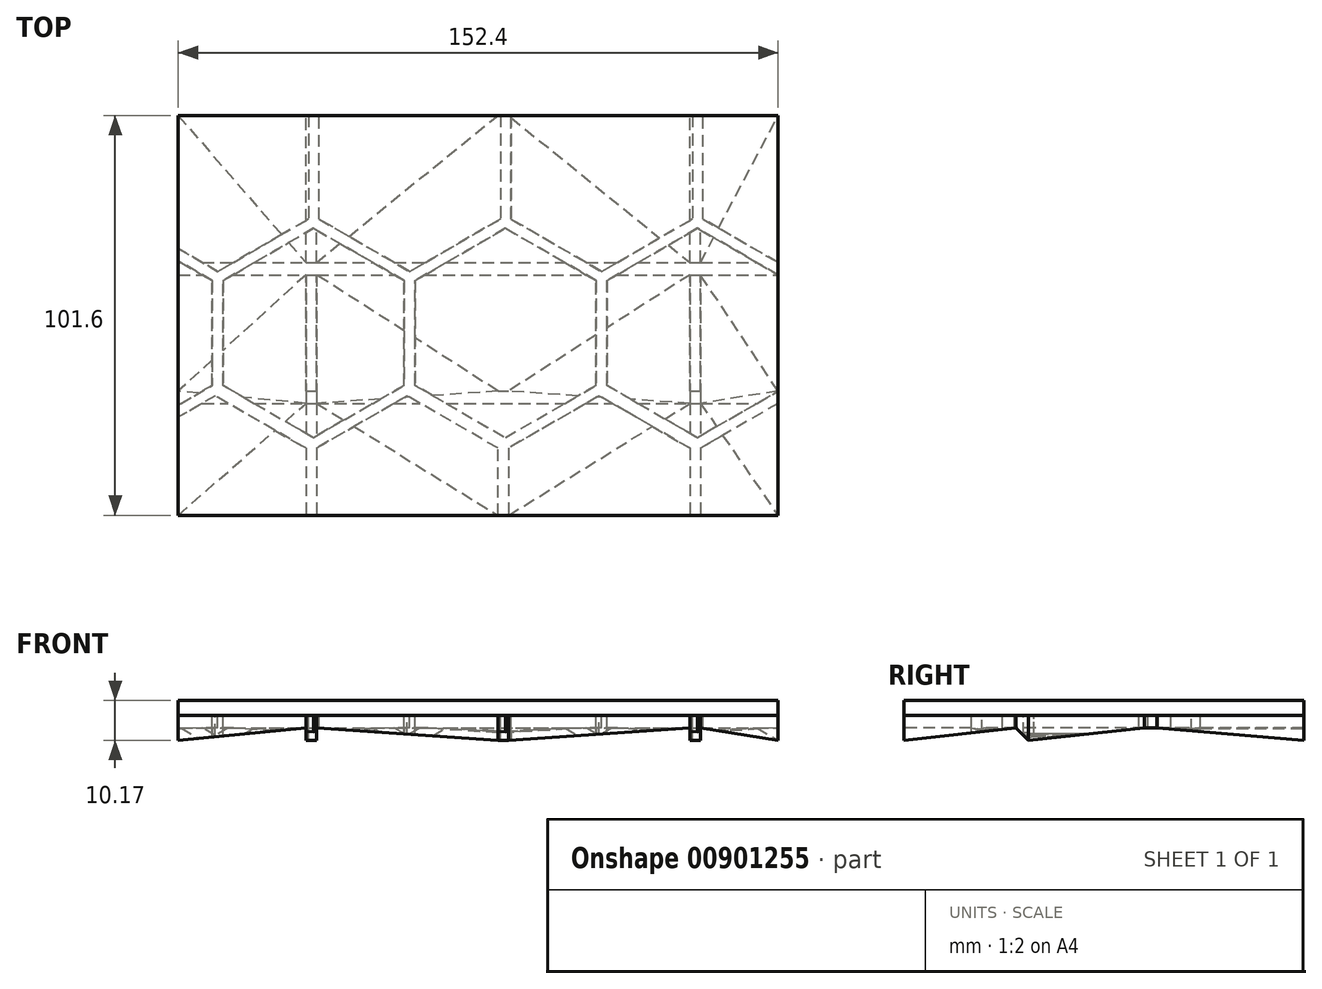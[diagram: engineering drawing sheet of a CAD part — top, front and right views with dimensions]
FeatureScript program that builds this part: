
annotation { "Feature Type Name" : "Feature", "Feature Type Description" : "" }
export const myFeature = defineFeature(function(context is Context, id is Id, definition is map)
    precondition{}
    {
        {
            var Q0;
            Q0=qCreatedBy(makeId("Top.planeOp"),FACE);
            var sketch = newSketch(context, id + "F0", { "sketchPlane" : qUnion([Q0])});
            skLineSegment(sketch, "E0.bottom", {"start": v(-65.42, 49.7) * mm, "end": v(86.98, 49.7) * mm});
            skLineSegment(sketch, "E0.top", {"start": v(-65.42, -51.9) * mm, "end": v(86.98, -51.9) * mm});
            skLineSegment(sketch, "E0.left", {"start": v(-65.42, 49.7) * mm, "end": v(-65.42, -51.9) * mm});
            skLineSegment(sketch, "E0.right", {"start": v(86.98, 49.7) * mm, "end": v(86.98, -51.9) * mm});
            skCircle(sketch, "E1", {"center": v(-62.35, 45.98) * mm, "radius": 11.46 * mm});
            skSolve(sketch);
        }
        {
            var Q0;
            {var subQ2=sQuery(id+"F0.wireOp",EDGE,"E0.top");Q0=makeQuery(id+"F0.imprint","IMPRINT",FACE,{"disambiguationData":[TD([[makeQuery(id+"F0.imprint","IMPRINT",EDGE,{"derivedFrom":subQ2}),1.0]])]});}
            var Q1;
            {var subQ0=sQuery(id+"F0.wireOp",EDGE,"E0.left");var subQ1=sQuery(id+"F0.wireOp",EDGE,"E0.bottom");var subQ2=makeQuery(id+"F0.imprint","INTERSECT",VERTEX,{"derivedFrom":[subQ1,subQ0]});Q1=makeQuery(id+"F0.imprint","IMPRINT",FACE,{"disambiguationData":[TD([[makeQuery(id+"F0.imprint","IMPRINT",EDGE,{"disambiguationData":[TD([[subQ2,-1.0]])],"derivedFrom":subQ1}),-1.0]])]});}
            extrude(context, id + "F1", {"entities" : qUnion([Q0, Q1]), "endBound" : BoundingType.SYMMETRIC, "oppositeDirection" : true, "depth" : 3.8 * mm, "offsetDistance" : 25.4 * mm});
        }
        {
            var Q0;
            Q0=makeQuery(id+"F1.opExtrude","CAP_FACE",FACE,{"disambiguationData":[OSD([sQuery(id+"F0.wireOp",EDGE,"E0.bottom"),sQuery(id+"F0.wireOp",EDGE,"E0.top"),sQuery(id+"F0.wireOp",EDGE,"E0.left"),sQuery(id+"F0.wireOp",EDGE,"E0.right")])],"isStart":false});
            var sketch = newSketch(context, id + "F2", { "sketchPlane" : qUnion([Q0])});
            skCircle(sketch, "E2.cCircle", {"center": v(-56.01, 48.13) * mm, "radius": 23.03 * mm, "construction": true});
            skLineSegment(sketch, "E2.0", {"start": v(-32.98, 34.83) * mm, "end": v(-56.01, 21.53) * mm});
            skLineSegment(sketch, "E2.1", {"start": v(-56.01, 21.53) * mm, "end": v(-79.04, 34.83) * mm});
            skLineSegment(sketch, "E2.2", {"start": v(-79.04, 34.83) * mm, "end": v(-79.04, 61.43) * mm});
            skLineSegment(sketch, "E2.3", {"start": v(-79.04, 61.43) * mm, "end": v(-56.01, 74.72) * mm});
            skLineSegment(sketch, "E2.4", {"start": v(-56.01, 74.72) * mm, "end": v(-32.98, 61.43) * mm});
            skLineSegment(sketch, "E2.5", {"start": v(-32.98, 61.43) * mm, "end": v(-32.98, 34.83) * mm});
            skPoint(sketch, "E2.0.midPoint", {"position": v(-44.5, 28.18) * mm});
            skLineSegment(sketch, "E3", {"start": v(-56.01, 48.13) * mm, "end": v(-56.01, 21.53) * mm});
            skLineSegment(sketch, "E4.0.1.0", {"start": v(-32.34, -49.95) * mm, "end": v(-55.37, -63.25) * mm});
            skLineSegment(sketch, "E4.0.1.1", {"start": v(-55.37, -63.25) * mm, "end": v(-78.4, -49.95) * mm});
            skLineSegment(sketch, "E4.0.1.2", {"start": v(-78.4, -49.95) * mm, "end": v(-78.4, -23.35) * mm});
            skLineSegment(sketch, "E4.0.1.3", {"start": v(-78.4, -23.35) * mm, "end": v(-55.37, -10.05) * mm});
            skLineSegment(sketch, "E4.0.1.4", {"start": v(-55.37, -10.05) * mm, "end": v(-32.34, -23.35) * mm});
            skLineSegment(sketch, "E4.0.1.5", {"start": v(-32.34, -23.35) * mm, "end": v(-32.34, -49.95) * mm});
            skLineSegment(sketch, "E4.1.0.0", {"start": v(15.79, 34.83) * mm, "end": v(-7.24, 21.53) * mm});
            skLineSegment(sketch, "E4.1.0.1", {"start": v(-7.24, 21.53) * mm, "end": v(-30.28, 34.83) * mm});
            skLineSegment(sketch, "E4.1.0.2", {"start": v(-30.28, 34.83) * mm, "end": v(-30.28, 61.43) * mm});
            skLineSegment(sketch, "E4.1.0.3", {"start": v(-30.28, 61.43) * mm, "end": v(-7.24, 74.72) * mm});
            skLineSegment(sketch, "E4.1.0.4", {"start": v(-7.24, 74.72) * mm, "end": v(15.79, 61.43) * mm});
            skLineSegment(sketch, "E4.1.0.5", {"start": v(15.79, 61.43) * mm, "end": v(15.79, 34.83) * mm});
            skLineSegment(sketch, "E4.1.1.0", {"start": v(16.43, -49.95) * mm, "end": v(-6.6, -63.25) * mm});
            skLineSegment(sketch, "E4.1.1.1", {"start": v(-6.6, -63.25) * mm, "end": v(-29.64, -49.95) * mm});
            skLineSegment(sketch, "E4.1.1.2", {"start": v(-29.64, -49.95) * mm, "end": v(-29.64, -23.35) * mm});
            skLineSegment(sketch, "E4.1.1.3", {"start": v(-29.64, -23.35) * mm, "end": v(-6.6, -10.05) * mm});
            skLineSegment(sketch, "E4.1.1.4", {"start": v(-6.6, -10.05) * mm, "end": v(16.43, -23.35) * mm});
            skLineSegment(sketch, "E4.1.1.5", {"start": v(16.43, -23.35) * mm, "end": v(16.43, -49.95) * mm});
            skLineSegment(sketch, "E4.2.0.0", {"start": v(64.56, 34.83) * mm, "end": v(41.52, 21.53) * mm});
            skLineSegment(sketch, "E4.2.0.1", {"start": v(41.52, 21.53) * mm, "end": v(18.5, 34.83) * mm});
            skLineSegment(sketch, "E4.2.0.2", {"start": v(18.5, 34.83) * mm, "end": v(18.5, 61.43) * mm});
            skLineSegment(sketch, "E4.2.0.3", {"start": v(18.5, 61.43) * mm, "end": v(41.52, 74.72) * mm});
            skLineSegment(sketch, "E4.2.0.4", {"start": v(41.52, 74.72) * mm, "end": v(64.56, 61.43) * mm});
            skLineSegment(sketch, "E4.2.0.5", {"start": v(64.56, 61.43) * mm, "end": v(64.56, 34.83) * mm});
            skLineSegment(sketch, "E4.2.1.0", {"start": v(65.2, -49.95) * mm, "end": v(42.16, -63.25) * mm});
            skLineSegment(sketch, "E4.2.1.1", {"start": v(42.16, -63.25) * mm, "end": v(19.13, -49.95) * mm});
            skLineSegment(sketch, "E4.2.1.2", {"start": v(19.13, -49.95) * mm, "end": v(19.13, -23.35) * mm});
            skLineSegment(sketch, "E4.2.1.3", {"start": v(19.13, -23.35) * mm, "end": v(42.16, -10.05) * mm});
            skLineSegment(sketch, "E4.2.1.4", {"start": v(42.16, -10.05) * mm, "end": v(65.2, -23.35) * mm});
            skLineSegment(sketch, "E4.2.1.5", {"start": v(65.2, -23.35) * mm, "end": v(65.2, -49.95) * mm});
            skLineSegment(sketch, "E4.3.0.0", {"start": v(113.33, 34.83) * mm, "end": v(90.3, 21.53) * mm});
            skLineSegment(sketch, "E4.3.0.1", {"start": v(90.3, 21.53) * mm, "end": v(67.26, 34.83) * mm});
            skLineSegment(sketch, "E4.3.0.2", {"start": v(67.26, 34.83) * mm, "end": v(67.26, 61.43) * mm});
            skLineSegment(sketch, "E4.3.0.3", {"start": v(67.26, 61.43) * mm, "end": v(90.3, 74.72) * mm});
            skLineSegment(sketch, "E4.3.0.4", {"start": v(90.3, 74.72) * mm, "end": v(113.33, 61.43) * mm});
            skLineSegment(sketch, "E4.3.0.5", {"start": v(113.33, 61.43) * mm, "end": v(113.33, 34.83) * mm});
            skLineSegment(sketch, "E4.3.1.0", {"start": v(113.97, -49.95) * mm, "end": v(90.93, -63.25) * mm});
            skLineSegment(sketch, "E4.3.1.1", {"start": v(90.93, -63.25) * mm, "end": v(67.9, -49.95) * mm});
            skLineSegment(sketch, "E4.3.1.2", {"start": v(67.9, -49.95) * mm, "end": v(67.9, -23.35) * mm});
            skLineSegment(sketch, "E4.3.1.3", {"start": v(67.9, -23.35) * mm, "end": v(90.93, -10.05) * mm});
            skLineSegment(sketch, "E4.3.1.4", {"start": v(90.93, -10.05) * mm, "end": v(113.97, -23.35) * mm});
            skLineSegment(sketch, "E4.3.1.5", {"start": v(113.97, -23.35) * mm, "end": v(113.97, -49.95) * mm});
            skLineSegment(sketch, "E4.direction1", {"start": v(-56.01, 21.53) * mm, "end": v(-7.24, 21.53) * mm, "construction": true});
            skLineSegment(sketch, "E4.direction2", {"start": v(-56.01, 21.53) * mm, "end": v(-55.37, -63.25) * mm, "construction": true});
            skCircle(sketch, "E5.cCircle", {"center": v(-79.8, 5.56) * mm, "radius": 23.03 * mm, "construction": true});
            skLineSegment(sketch, "E5.0", {"start": v(-56.77, -7.74) * mm, "end": v(-79.8, -21.04) * mm});
            skLineSegment(sketch, "E5.1", {"start": v(-79.8, -21.04) * mm, "end": v(-102.83, -7.74) * mm});
            skLineSegment(sketch, "E5.2", {"start": v(-102.83, -7.74) * mm, "end": v(-102.83, 18.86) * mm});
            skLineSegment(sketch, "E5.3", {"start": v(-102.83, 18.86) * mm, "end": v(-79.8, 32.16) * mm});
            skLineSegment(sketch, "E5.4", {"start": v(-79.8, 32.16) * mm, "end": v(-56.77, 18.86) * mm});
            skLineSegment(sketch, "E5.5", {"start": v(-56.77, 18.86) * mm, "end": v(-56.77, -7.74) * mm});
            skPoint(sketch, "E5.0.midPoint", {"position": v(-68.28, -14.39) * mm});
            skLineSegment(sketch, "E6", {"start": v(-79.8, 5.56) * mm, "end": v(-79.8, -21.04) * mm});
            skLineSegment(sketch, "E7", {"start": v(-68.28, 25.5) * mm, "end": v(-66.93, 27.85) * mm});
            skLineSegment(sketch, "E8", {"start": v(-68.28, -14.39) * mm, "end": v(-66.93, -16.73) * mm});
            skLineSegment(sketch, "E9", {"start": v(-30.28, 48.13) * mm, "end": v(-32.98, 48.13) * mm});
            skLineSegment(sketch, "E10.1.0.0", {"start": v(-31.03, 32.16) * mm, "end": v(-8, 18.86) * mm});
            skLineSegment(sketch, "E10.1.0.1", {"start": v(-8, 18.86) * mm, "end": v(-8, -7.74) * mm});
            skLineSegment(sketch, "E10.1.0.2", {"start": v(-8, -7.74) * mm, "end": v(-31.03, -21.04) * mm});
            skLineSegment(sketch, "E10.1.0.3", {"start": v(-31.03, -21.04) * mm, "end": v(-54.06, -7.74) * mm});
            skLineSegment(sketch, "E10.1.0.4", {"start": v(-54.06, -7.74) * mm, "end": v(-54.06, 18.86) * mm});
            skLineSegment(sketch, "E10.1.0.5", {"start": v(-54.06, 18.86) * mm, "end": v(-31.03, 32.16) * mm});
            skLineSegment(sketch, "E10.2.0.0", {"start": v(17.74, 32.16) * mm, "end": v(40.77, 18.86) * mm});
            skLineSegment(sketch, "E10.2.0.1", {"start": v(40.77, 18.86) * mm, "end": v(40.77, -7.74) * mm});
            skLineSegment(sketch, "E10.2.0.2", {"start": v(40.77, -7.74) * mm, "end": v(17.74, -21.04) * mm});
            skLineSegment(sketch, "E10.2.0.3", {"start": v(17.74, -21.04) * mm, "end": v(-5.3, -7.74) * mm});
            skLineSegment(sketch, "E10.2.0.4", {"start": v(-5.3, -7.74) * mm, "end": v(-5.3, 18.86) * mm});
            skLineSegment(sketch, "E10.2.0.5", {"start": v(-5.3, 18.86) * mm, "end": v(17.74, 32.16) * mm});
            skLineSegment(sketch, "E10.3.0.0", {"start": v(66.5, 32.16) * mm, "end": v(89.54, 18.86) * mm});
            skLineSegment(sketch, "E10.3.0.1", {"start": v(89.54, 18.86) * mm, "end": v(89.54, -7.74) * mm});
            skLineSegment(sketch, "E10.3.0.2", {"start": v(89.54, -7.74) * mm, "end": v(66.5, -21.04) * mm});
            skLineSegment(sketch, "E10.3.0.3", {"start": v(66.5, -21.04) * mm, "end": v(43.47, -7.74) * mm});
            skLineSegment(sketch, "E10.3.0.4", {"start": v(43.47, -7.74) * mm, "end": v(43.47, 18.86) * mm});
            skLineSegment(sketch, "E10.3.0.5", {"start": v(43.47, 18.86) * mm, "end": v(66.5, 32.16) * mm});
            skLineSegment(sketch, "E10.direction1", {"start": v(-79.8, 32.16) * mm, "end": v(-31.03, 32.16) * mm, "construction": true});
            skLineSegment(sketch, "E11.0", {"start": v(-65.42, 51.9) * mm, "end": v(86.98, 51.9) * mm});
            skLineSegment(sketch, "E12.0", {"start": v(-65.42, -49.7) * mm, "end": v(-65.42, 51.9) * mm});
            skLineSegment(sketch, "E13.0", {"start": v(-65.42, -49.7) * mm, "end": v(86.98, -49.7) * mm});
            skLineSegment(sketch, "E14.0", {"start": v(86.98, -49.7) * mm, "end": v(86.98, 51.9) * mm});
            skSolve(sketch);
        }
        {
            var Q0;
            {var subQ1=sQuery(id+"F2.wireOp",EDGE,"E2.0");Q0=makeQuery(id+"F2.imprint","IMPRINT",FACE,{"disambiguationData":[TD([[makeQuery(id+"F2.imprint","IMPRINT",EDGE,{"derivedFrom":subQ1}),-1.0]])]});}
            var Q1;
            {var subQ0=sQuery(id+"F2.wireOp",EDGE,"E5.5");Q1=makeQuery(id+"F2.imprint","IMPRINT",FACE,{"disambiguationData":[TD([[makeQuery(id+"F2.imprint","IMPRINT",EDGE,{"derivedFrom":subQ0}),-1.0]])]});}
            var Q2;
            {var subQ6=sQuery(id+"F2.wireOp",EDGE,"E4.0.1.4");Q2=makeQuery(id+"F2.imprint","IMPRINT",FACE,{"disambiguationData":[TD([[makeQuery(id+"F2.imprint","IMPRINT",EDGE,{"derivedFrom":subQ6}),-1.0]])]});}
            var Q3;
            Q3=makeQuery(id+"F2.imprint","IMPRINT",FACE,{"disambiguationData":[TD([[makeQuery(id+"F2.imprint","IMPRINT",EDGE,{"derivedFrom":sQuery(id+"F2.wireOp",EDGE,"E10.1.0.0")}),-1.0]])]});
            var Q4;
            {var subQ5=sQuery(id+"F2.wireOp",EDGE,"E4.1.0.0");Q4=makeQuery(id+"F2.imprint","IMPRINT",FACE,{"disambiguationData":[TD([[makeQuery(id+"F2.imprint","IMPRINT",EDGE,{"derivedFrom":subQ5}),-1.0]])]});}
            var Q5;
            Q5=makeQuery(id+"F2.imprint","IMPRINT",FACE,{"disambiguationData":[TD([[makeQuery(id+"F2.imprint","IMPRINT",EDGE,{"derivedFrom":sQuery(id+"F2.wireOp",EDGE,"E10.2.0.0")}),-1.0]])]});
            var Q6;
            {var subQ4=sQuery(id+"F2.wireOp",EDGE,"E4.1.1.3");Q6=makeQuery(id+"F2.imprint","IMPRINT",FACE,{"disambiguationData":[TD([[makeQuery(id+"F2.imprint","IMPRINT",EDGE,{"derivedFrom":subQ4}),-1.0]])]});}
            var Q7;
            {var subQ4=sQuery(id+"F2.wireOp",EDGE,"E4.2.1.3");Q7=makeQuery(id+"F2.imprint","IMPRINT",FACE,{"disambiguationData":[TD([[makeQuery(id+"F2.imprint","IMPRINT",EDGE,{"derivedFrom":subQ4}),-1.0]])]});}
            var Q8;
            {var subQ0=sQuery(id+"F2.wireOp",EDGE,"E10.3.0.3");Q8=makeQuery(id+"F2.imprint","IMPRINT",FACE,{"disambiguationData":[TD([[makeQuery(id+"F2.imprint","IMPRINT",EDGE,{"derivedFrom":subQ0}),-1.0]])]});}
            var Q9;
            {var subQ1=sQuery(id+"F2.wireOp",EDGE,"E4.2.0.0");Q9=makeQuery(id+"F2.imprint","IMPRINT",FACE,{"disambiguationData":[TD([[makeQuery(id+"F2.imprint","IMPRINT",EDGE,{"derivedFrom":subQ1}),-1.0]])]});}
            var Q10;
            {var subQ0=sQuery(id+"F2.wireOp",EDGE,"E4.3.0.2");var subQ1=sQuery(id+"F2.wireOp",EDGE,"E4.3.0.1");var subQ2=makeQuery(id+"F2.imprint","INTERSECT",VERTEX,{"derivedFrom":[subQ1,subQ0]});Q10=makeQuery(id+"F2.imprint","IMPRINT",FACE,{"disambiguationData":[TD([[makeQuery(id+"F2.imprint","IMPRINT",EDGE,{"disambiguationData":[TD([[subQ2,1.0]])],"derivedFrom":subQ1}),-1.0]])]});}
            var Q11;
            {var subQ0=sQuery(id+"F2.wireOp",EDGE,"E4.3.1.3");var subQ1=sQuery(id+"F2.wireOp",EDGE,"E4.3.1.2");var subQ2=makeQuery(id+"F2.imprint","INTERSECT",VERTEX,{"derivedFrom":[subQ1,subQ0]});Q11=makeQuery(id+"F2.imprint","IMPRINT",FACE,{"disambiguationData":[TD([[makeQuery(id+"F2.imprint","IMPRINT",EDGE,{"disambiguationData":[TD([[subQ2,1.0]])],"derivedFrom":subQ1}),-1.0]])]});}
            extrude(context, id + "F3", {"entities" : qUnion([Q0, Q1, Q2, Q3, Q4, Q5, Q6, Q7, Q8, Q9, Q10, Q11]), "depth" : 6.35 * mm, "offsetDistance" : 25.4 * mm});
        }
        {
            var Q0;
            Q0=makeQuery(id+"F1.opExtrude","SWEPT_FACE",FACE,{"disambiguationData":[OSD([sQuery(id+"F0.wireOp",EDGE,"E0.top")])]});
            var sketch = newSketch(context, id + "F4", { "sketchPlane" : qUnion([Q0])});
            skLineSegment(sketch, "E15.0", {"start": v(86.98, -8.26) * mm, "end": v(86.98, -1.9) * mm});
            skLineSegment(sketch, "E16.0", {"start": v(67.26, -8.26) * mm, "end": v(86.98, -8.26) * mm});
            skLineSegment(sketch, "E17.0", {"start": v(-65.42, -8.26) * mm, "end": v(-32.98, -8.26) * mm});
            skLineSegment(sketch, "E18.0", {"start": v(-65.42, -8.26) * mm, "end": v(-65.42, -1.9) * mm});
            skLineSegment(sketch, "E19.0", {"start": v(-65.42, 1.9) * mm, "end": v(86.98, 1.9) * mm});
            skPoint(sketch, "E20.0", {"position": v(-65.42, 0) * mm});
            skLineSegment(sketch, "E21.0", {"start": v(-65.42, -1.9) * mm, "end": v(-65.42, 1.9) * mm});
            skLineSegment(sketch, "E22.0", {"start": v(86.98, -1.9) * mm, "end": v(86.98, 1.9) * mm});
            skLineSegment(sketch, "E23.0", {"start": v(67.26, -8.26) * mm, "end": v(67.26, -1.9) * mm});
            skLineSegment(sketch, "E24.0", {"start": v(64.56, -8.26) * mm, "end": v(64.56, -1.9) * mm});
            skLineSegment(sketch, "E25.0", {"start": v(18.5, -8.26) * mm, "end": v(18.5, -1.9) * mm});
            skLineSegment(sketch, "E26.0", {"start": v(15.79, -8.26) * mm, "end": v(15.79, -1.9) * mm});
            skLineSegment(sketch, "E27.0", {"start": v(-30.28, -8.26) * mm, "end": v(-30.28, -1.9) * mm});
            skLineSegment(sketch, "E28.0", {"start": v(-32.98, -8.26) * mm, "end": v(-32.98, -1.9) * mm});
            skLineSegment(sketch, "E29.0", {"start": v(-30.28, -8.26) * mm, "end": v(15.79, -8.26) * mm});
            skLineSegment(sketch, "E30.0", {"start": v(18.5, -8.26) * mm, "end": v(64.56, -8.26) * mm});
            skLineSegment(sketch, "E31.0", {"start": v(18.5, -1.9) * mm, "end": v(64.56, -1.9) * mm});
            skLineSegment(sketch, "E32.0", {"start": v(-30.28, -1.9) * mm, "end": v(15.79, -1.9) * mm});
            skLineSegment(sketch, "E33.0", {"start": v(-65.42, -1.9) * mm, "end": v(86.98, -1.9) * mm});
            skLineSegment(sketch, "E34", {"start": v(86.98, -8.26) * mm, "end": v(67.26, -5.08) * mm});
            skLineSegment(sketch, "E35", {"start": v(64.56, -5.08) * mm, "end": v(18.5, -8.25) * mm});
            skLineSegment(sketch, "E36", {"start": v(15.79, -8.25) * mm, "end": v(-30.28, -5.08) * mm});
            skLineSegment(sketch, "E37", {"start": v(-32.98, -5.08) * mm, "end": v(-65.42, -8.26) * mm});
            skLineSegment(sketch, "E38.0", {"start": v(43.47, -8.26) * mm, "end": v(66.5, -8.26) * mm});
            skPoint(sketch, "E39.0", {"position": v(67.26, -8.26) * mm});
            skLineSegment(sketch, "E40.0", {"start": v(66.5, -8.26) * mm, "end": v(86.98, -8.26) * mm});
            skLineSegment(sketch, "E41.0", {"start": v(17.74, -8.26) * mm, "end": v(40.77, -8.26) * mm});
            skLineSegment(sketch, "E42.0", {"start": v(-5.3, -8.26) * mm, "end": v(17.74, -8.26) * mm});
            skSolve(sketch);
        }
        {
            var Q0;
            Q0=makeQuery(id+"F1.opExtrude","SWEPT_FACE",FACE,{"disambiguationData":[OSD([sQuery(id+"F0.wireOp",EDGE,"E0.right")])]});
            var sketch = newSketch(context, id + "F5", { "sketchPlane" : qUnion([Q0])});
            skLineSegment(sketch, "E43.0", {"start": v(49.7, -8.26) * mm, "end": v(49.7, -1.9) * mm});
            skLineSegment(sketch, "E44.0", {"start": v(49.7, -8.26) * mm, "end": v(12.34, -8.26) * mm});
            skLineSegment(sketch, "E45.0", {"start": v(9.22, -8.26) * mm, "end": v(-20.34, -8.26) * mm});
            skLineSegment(sketch, "E46.0", {"start": v(-23.44, -8.26) * mm, "end": v(-51.9, -8.26) * mm});
            skLineSegment(sketch, "E47.0", {"start": v(-51.9, -8.26) * mm, "end": v(-51.9, -1.9) * mm});
            skLineSegment(sketch, "E48.0", {"start": v(-51.9, -1.9) * mm, "end": v(-51.9, 1.9) * mm});
            skLineSegment(sketch, "E49.0", {"start": v(49.7, 1.9) * mm, "end": v(-51.9, 1.9) * mm});
            skLineSegment(sketch, "E50.0", {"start": v(49.7, -1.9) * mm, "end": v(49.7, 1.9) * mm});
            skPoint(sketch, "E51.0", {"position": v(12.34, -5.08) * mm});
            skLineSegment(sketch, "E52.0", {"start": v(12.34, -8.26) * mm, "end": v(12.34, -1.9) * mm});
            skLineSegment(sketch, "E53.0", {"start": v(9.22, -8.26) * mm, "end": v(9.22, -1.9) * mm});
            skLineSegment(sketch, "E54.0", {"start": v(-20.34, -8.26) * mm, "end": v(-20.34, -1.9) * mm});
            skLineSegment(sketch, "E55.0", {"start": v(-23.44, -8.26) * mm, "end": v(-23.44, -1.9) * mm});
            skLineSegment(sketch, "E56", {"start": v(49.7, -8.25) * mm, "end": v(12.34, -5.08) * mm});
            skLineSegment(sketch, "E57", {"start": v(9.22, -5.08) * mm, "end": v(-20.34, -8.26) * mm});
            skLineSegment(sketch, "E58", {"start": v(-51.9, -8.26) * mm, "end": v(-23.44, -5.08) * mm});
            skLineSegment(sketch, "E59", {"start": v(12.34, -5.08) * mm, "end": v(9.22, -5.08) * mm});
            skLineSegment(sketch, "E60", {"start": v(-23.44, -5.08) * mm, "end": v(-20.34, -8.26) * mm});
            skLineSegment(sketch, "E61.0", {"start": v(9.22, -8.26) * mm, "end": v(21.04, -8.26) * mm});
            skLineSegment(sketch, "E62.0", {"start": v(-32.16, -8.26) * mm, "end": v(-20.34, -8.26) * mm});
            skSolve(sketch);
        }
        {
            var Q0;
            {var subQ0=sQuery(id+"F5.wireOp",EDGE,"E44.0");Q0=makeQuery(id+"F5.imprint","IMPRINT",FACE,{"disambiguationData":[TD([[makeQuery(id+"F5.imprint","IMPRINT",EDGE,{"derivedFrom":subQ0}),-1.0]])]});}
            var Q1;
            {var subQ0=sQuery(id+"F5.wireOp",EDGE,"E45.0");Q1=makeQuery(id+"F5.imprint","IMPRINT",FACE,{"disambiguationData":[TD([[makeQuery(id+"F5.imprint","IMPRINT",EDGE,{"derivedFrom":subQ0}),-1.0]])]});}
            var Q2;
            {var subQ0=sQuery(id+"F5.wireOp",EDGE,"E46.0");Q2=makeQuery(id+"F5.imprint","IMPRINT",FACE,{"disambiguationData":[TD([[makeQuery(id+"F5.imprint","IMPRINT",EDGE,{"derivedFrom":subQ0}),-1.0]])]});}
            var Q3;
            {var subQ3=sQuery(id+"F5.wireOp",EDGE,"E59");Q3=makeQuery(id+"F5.imprint","IMPRINT",FACE,{"disambiguationData":[TD([[makeQuery(id+"F5.imprint","IMPRINT",EDGE,{"derivedFrom":subQ3}),1.0]])]});}
            var Q4;
            {var subQ3=sQuery(id+"F5.wireOp",EDGE,"E60");Q4=makeQuery(id+"F5.imprint","IMPRINT",FACE,{"disambiguationData":[TD([[makeQuery(id+"F5.imprint","IMPRINT",EDGE,{"derivedFrom":subQ3}),-1.0]])]});}
            extrude(context, id + "F6", {"entities" : qUnion([Q0, Q1, Q2, Q3, Q4]), "operationType" : NewBodyOperationType.REMOVE, "endBound" : BoundingType.THROUGH_ALL, "oppositeDirection" : true, "depth" : 25.4 * mm, "offsetDistance" : 25.4 * mm});
        }
        {
            var Q0;
            {var subQ3=sQuery(id+"F4.wireOp",EDGE,"E34");Q0=makeQuery(id+"F4.imprint","IMPRINT",FACE,{"disambiguationData":[TD([[makeQuery(id+"F4.imprint","IMPRINT",EDGE,{"derivedFrom":subQ3}),1.0]])]});}
            var Q1;
            {var subQ3=sQuery(id+"F4.wireOp",EDGE,"E30.0");Q1=makeQuery(id+"F4.imprint","IMPRINT",FACE,{"disambiguationData":[TD([[makeQuery(id+"F4.imprint","IMPRINT",EDGE,{"derivedFrom":subQ3}),1.0]])]});}
            var Q2;
            {var subQ0=sQuery(id+"F4.wireOp",EDGE,"E29.0");Q2=makeQuery(id+"F4.imprint","IMPRINT",FACE,{"disambiguationData":[TD([[makeQuery(id+"F4.imprint","IMPRINT",EDGE,{"derivedFrom":subQ0}),1.0]])]});}
            var Q3;
            {var subQ0=sQuery(id+"F4.wireOp",EDGE,"E17.0");Q3=makeQuery(id+"F4.imprint","IMPRINT",FACE,{"disambiguationData":[TD([[makeQuery(id+"F4.imprint","IMPRINT",EDGE,{"derivedFrom":subQ0}),1.0]])]});}
            extrude(context, id + "F7", {"entities" : qUnion([Q0, Q1, Q2, Q3]), "operationType" : NewBodyOperationType.REMOVE, "endBound" : BoundingType.THROUGH_ALL, "oppositeDirection" : true, "depth" : 25.4 * mm, "offsetDistance" : 25.4 * mm});
        }
    });
